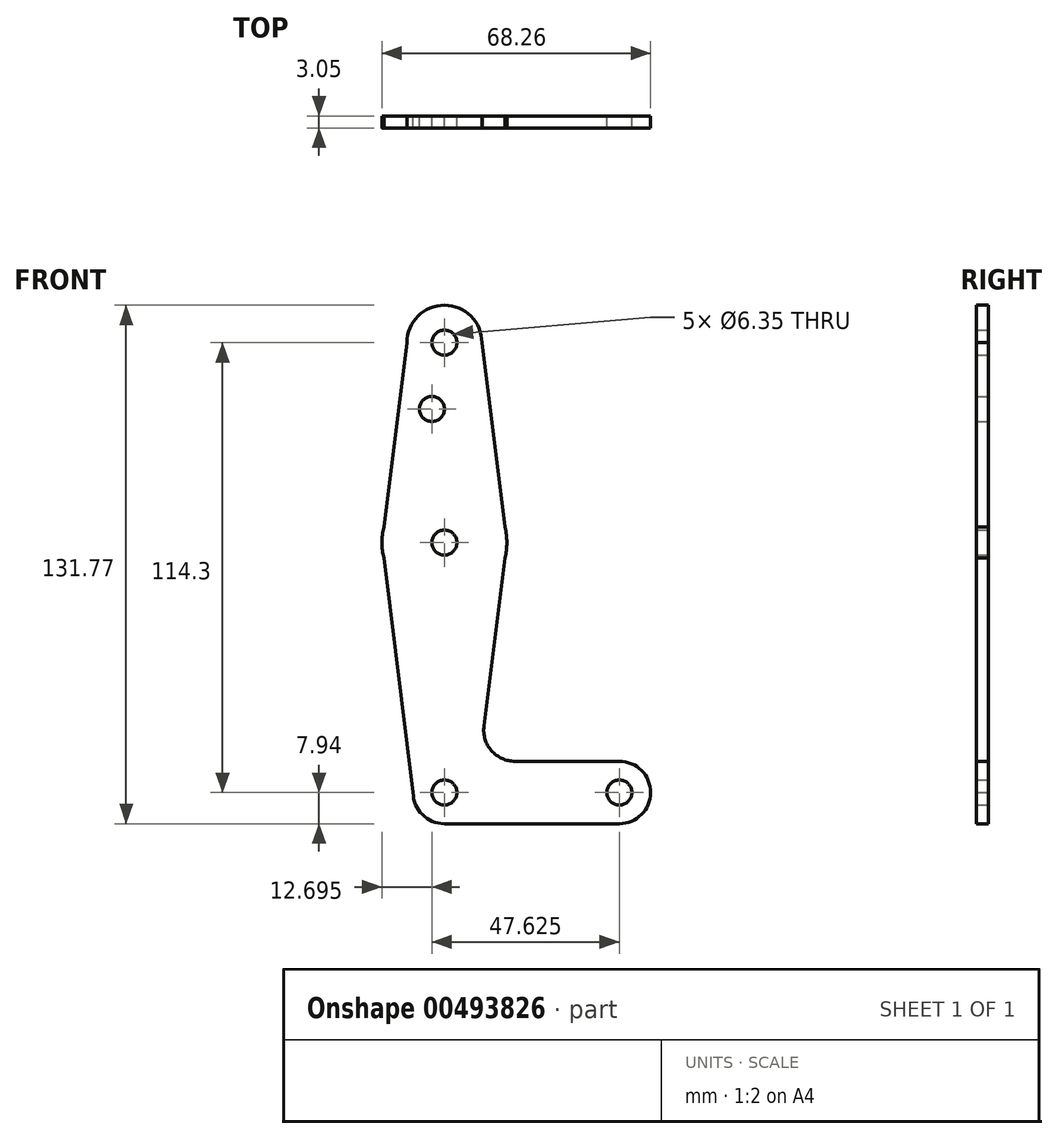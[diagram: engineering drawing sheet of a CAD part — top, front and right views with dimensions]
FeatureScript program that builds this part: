
annotation { "Feature Type Name" : "Feature", "Feature Type Description" : "" }
export const myFeature = defineFeature(function(context is Context, id is Id, definition is map)
    precondition{}
    {
        {
            var Q0;
            Q0=qCreatedBy(makeId("Front.planeOp"),FACE);
            var sketch = newSketch(context, id + "F0", { "sketchPlane" : qUnion([Q0])});
            skCircle(sketch, "E0", {"center": v(0, 0) * mm, "radius": 7.94 * mm});
            skLineSegment(sketch, "E1", {"start": v(0, 0) * mm, "end": v(0, 114.3) * mm, "construction": true});
            skLineSegment(sketch, "E2", {"start": v(0, 0) * mm, "end": v(44.45, 0) * mm, "construction": true});
            skCircle(sketch, "E3", {"center": v(0, 114.3) * mm, "radius": 9.53 * mm});
            skCircle(sketch, "E4", {"center": v(44.45, 0) * mm, "radius": 7.94 * mm});
            skCircle(sketch, "E5", {"center": v(0, 63.5) * mm, "radius": 15.88 * mm});
            skLineSegment(sketch, "E6", {"start": v(9.52, 114.3) * mm, "end": v(15.88, 63.5) * mm});
            skLineSegment(sketch, "E7", {"start": v(15.88, 63.5) * mm, "end": v(10.05, 16.87) * mm});
            skLineSegment(sketch, "E8", {"start": v(-9.52, 114.3) * mm, "end": v(-15.88, 63.5) * mm});
            skLineSegment(sketch, "E9", {"start": v(-15.88, 63.5) * mm, "end": v(-7.94, 0) * mm});
            skLineSegment(sketch, "E10", {"start": v(0, -7.94) * mm, "end": v(44.45, -7.94) * mm});
            skLineSegment(sketch, "E11", {"start": v(17.94, 7.94) * mm, "end": v(44.45, 7.94) * mm});
            skCircle(sketch, "E12", {"center": v(-3.18, 97.44) * mm, "radius": 3.18 * mm});
            skCircle(sketch, "E13", {"center": v(0, 114.3) * mm, "radius": 3.18 * mm});
            skCircle(sketch, "E14", {"center": v(0, 63.5) * mm, "radius": 3.18 * mm});
            skCircle(sketch, "E15", {"center": v(0, 0) * mm, "radius": 3.18 * mm});
            skCircle(sketch, "E16", {"center": v(44.45, 0) * mm, "radius": 3.18 * mm});
            skArc(sketch, "E17.filletArc", {"start": v(10.05, 16.87) * mm, "mid": v(11.98, 10.63) * mm, "end": v(17.94, 7.94) * mm});
            skSolve(sketch);
        }
        {
            var Q0;
            Q0 = qSketchRegion(id + "F0", true);
            extrude(context, id + "F1", {"entities" : qUnion([Q0]), "depth" : 3.05 * mm});
        }
    });
